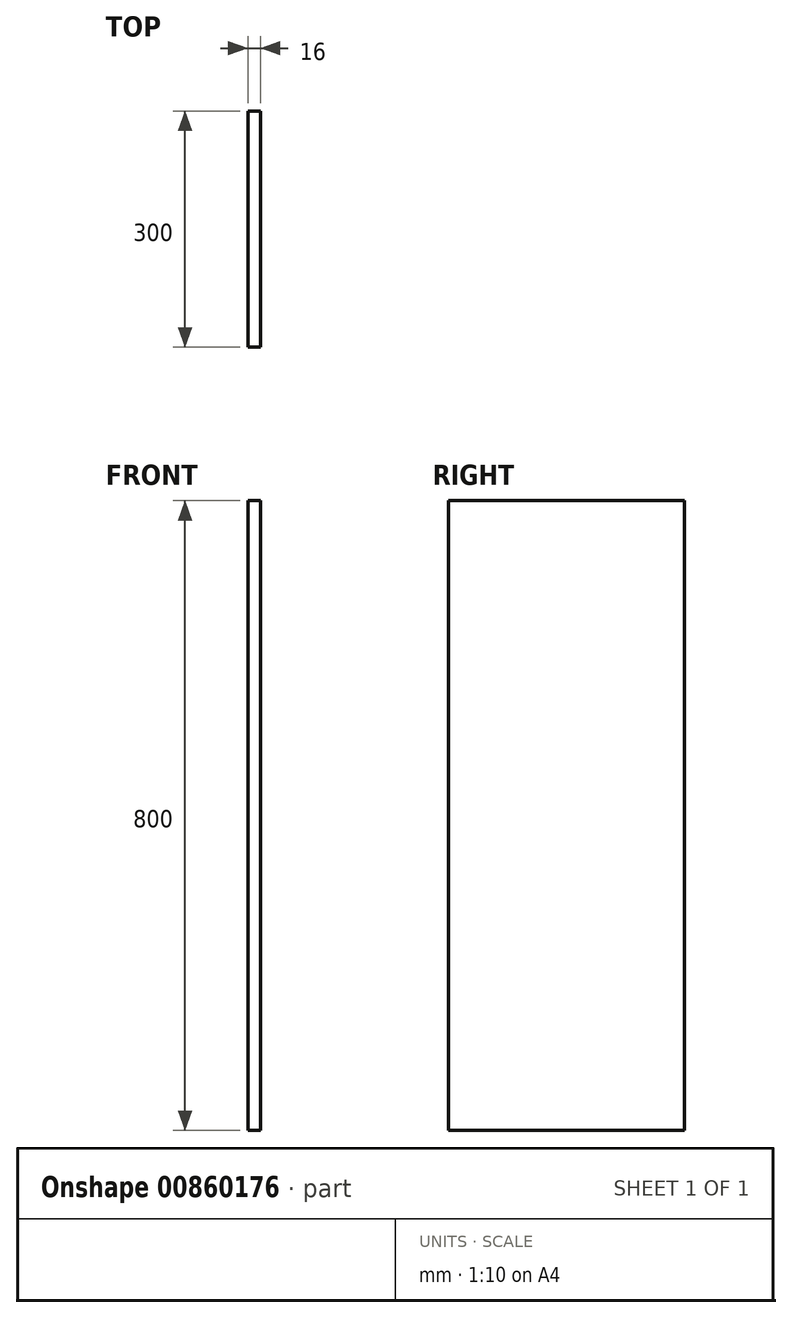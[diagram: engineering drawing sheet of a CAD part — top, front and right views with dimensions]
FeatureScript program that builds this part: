
annotation { "Feature Type Name" : "Feature", "Feature Type Description" : "" }
export const myFeature = defineFeature(function(context is Context, id is Id, definition is map)
    precondition{}
    {
        {
            var Q0;
            Q0=qCreatedBy(makeId("Front.planeOp"),FACE);
            var sketch = newSketch(context, id + "F0", { "sketchPlane" : qUnion([Q0])});
            skLineSegment(sketch, "E0.bottom", {"start": v(0, 0) * mm, "end": v(-16, 0) * mm});
            skLineSegment(sketch, "E0.top", {"start": v(0, 800) * mm, "end": v(-16, 800) * mm});
            skLineSegment(sketch, "E0.left", {"start": v(0, 0) * mm, "end": v(0, 800) * mm});
            skLineSegment(sketch, "E0.right", {"start": v(-16, 0) * mm, "end": v(-16, 800) * mm});
            skSolve(sketch);
        }
        {
            var Q0;
            Q0 = qSketchRegion(id + "F0", true);
            extrude(context, id + "F1", {"entities" : qUnion([Q0]), "depth" : 300 * mm, "offsetDistance" : 25 * mm});
        }
    });
